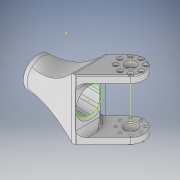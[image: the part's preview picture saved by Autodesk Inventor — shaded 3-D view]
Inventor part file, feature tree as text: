
AUTODESK INVENTOR PART (.ipt)
format: ipt  version: 2019 (Build 230136000, 136)  size: 1,101,312 bytes
history: native  units: mm
features: sketch x23, projected_geometry x19, extrude x16, plane x7, mirror x4, chamfer x4, fillet x4, other x4, loft x2, reference x2, pattern_circular x1, thicken_offset x1
ambient origin geometry x8: Origin, YZ Plane, XZ Plane, XY Plane, X Axis, Y Axis, Z Axis, Center Point
bodies: Solid1 (feature_tree)
feature tree (87):
  plane  "Work Plane1"
  plane  "Work Plane2"
  extrude  "Extrusion1"  Depth=23.0mm
  plane  "Work Plane5"
  extrude  "Extrusion2"  Depth=2.2mm
  extrude  "Extrusion3"  Depth=2.2mm
  mirror  "Mirror1"
  extrude  "Extrusion6"  Depth=2.2mm
  extrude  "Extrusion5"  Depth=2.2mm
  extrude  "Extrusion7"  Depth=7.0mm TaperAngle=0.0deg
  mirror  "Mirror2"
  extrude  "Extrusion8"  Depth=40.0mm
  extrude  "Extrusion9"  Depth=40.0mm
  mirror  "Mirror3"
  sketch  "Sketch10"  dims[d41=4.0mm d42=2.8mm]
  plane  "Work Plane8"
  extrude  "Extrusion11"  Depth=2.8mm
  extrude  "Extrusion12"  Depth=2.8mm
  extrude  "Extrusion13"  Depth=2.8mm
  sketch  "Sketch19"  dims[d49=2.8mm d50=2.0mm d51=0.0mm]
  plane  "Work Plane10"
  plane  "Work Plane9"
  sketch  "Sketch22"  dims[d52=45.5mm d53=4.0mm]
  sketch  "Sketch23"  dims[d54=45.5mm]
  plane  "Work Plane11"
  loft  "Loft3"
  extrude  "Extrusion15"  Depth=2.0mm TaperAngle=0.0deg
  extrude  "Extrusion16"  Depth=4.0mm
  chamfer  "Chamfer1"  Distance=4.0mm
  fillet  "Fillet17"  Radius=2.0mm
  fillet  "Fillet20"  Radius=5.2mm
  chamfer  "Chamfer2"  Distance=2.0mm
  fillet  "Fillet22"  Radius=2.5mm
  other  "Work Axis1"
  pattern_circular  "Circular Pattern1"  Angle=135.0deg  [1 undecoded]
  mirror  "Mirror4"
  extrude  "Extrusion17"  Depth=10.0mm
  chamfer  "Chamfer3"  Distance=5.2mm
  thicken_offset  "Thicken2"
  extrude  "Extrusion19"  Depth=10.0mm
  sketch  "Sketch31"  dims[d66=5.2mm]
  sketch  "Sketch32"  dims[d67=5.2mm]
  loft  "Loft4"
  extrude  "Extrusion21"  Depth=10.0mm
  fillet  "Fillet25"  Radius=5.5mm
  chamfer  "Chamfer4"  Distance=2.0mm
  sketch  "Sketch1"  dims[d0=44.5mm d1=23.0mm]
  sketch  "Sketch2"  dims[d2=2.2mm d3=2.2mm]
  projected_geometry  "Projected Loop1"
  sketch  "Sketch3"  dims[d4=2.2mm d5=2.2mm]
  projected_geometry  "Projected Loop2"
  sketch  "Sketch5"  dims[d6=2.2mm d7=2.2mm]
  reference  "Reference9"
  sketch  "Sketch6"  dims[d8=2.2mm d9=2.2mm]
  projected_geometry  "Projected Loop3"
  sketch  "Sketch7"  dims[d10=4.0mm d11=0.0mm d17=7.0mm d18=0.0mm]
  projected_geometry  "Projected Loop4"
  projected_geometry  "Projected Loop5"
  projected_geometry  "Projected Loop6"
  sketch  "Sketch8"  dims[d25=2.0mm d26=0.0mm d38=40.0mm]
  reference  "Reference10"
  projected_geometry  "Projected Loop7"
  projected_geometry  "Projected Loop8"
  sketch  "Sketch9"  dims[d39=4.0mm d40=40.0mm]
  projected_geometry  "Projected Loop9"
  projected_geometry  "Projected Loop10"
  sketch  "Sketch11"  dims[d43=2.8mm d44=2.8mm]
  projected_geometry  "Projected Loop11"
  projected_geometry  "Projected Loop12"
  sketch  "Sketch12"  dims[d45=2.8mm d46=2.8mm]
  projected_geometry  "Projected Loop13"
  sketch  "Sketch13"  dims[d47=2.8mm d48=2.8mm]
  projected_geometry  "Projected Loop14"
  sketch  "Sketch26"  dims[d55=4.0mm d56=4.0mm d57=0.0mm d58=2.0mm d59=0.0mm d61=5.2mm]
  other  "Edges3"
  sketch  "Sketch27"  dims[d62=5.2mm]
  projected_geometry  "Projected Loop18"
  sketch  "Sketch28"  dims[d63=5.2mm]
  projected_geometry  "Projected Loop19"
  sketch  "Sketch29"  dims[d64=5.2mm]
  sketch  "Sketch30"  dims[d65=5.2mm]
  other  "Edges4"
  other  "Edges5"
  sketch  "Sketch34"  dims[d68=5.2mm d69=2.0mm d70=0.0mm d71=2.5mm d78=135.0deg d79=5.2mm d80=5.2mm d81=5.2mm d82=5.2mm d83=5.2mm d85=5.5mm d86=2.0mm d87=20.0mm d88=14.827mm d89=40.0mm d90=10.0mm d91=0.0mm d92=27.2mm d93=31.0mm d96=4.0mm d97=0.0mm d98=4.0mm d99=0.0mm d100=4.0mm d101=0.0mm d131=-25.0mm d144=30.0mm d145=28.0mm d146=0.0mm d147=90.0deg d148=0.0mm d149=90.0deg d150=0.0mm d151=90.0deg d154=10.0mm d155=0.0mm d156=10.0mm d157=0.0mm d158=2.0mm d159=2.0mm d160=45.0deg d162=3.0mm d165=1.0mm d167=4.0mm d168=2.0mm d169=45.0deg d170=6.0mm d173=20.0mm d174=360.0deg d178=11.2mm d179=10.0mm d180=0.0mm d181=1.0mm d182=2.0mm d183=45.0deg d185=1.0mm d186=1.0mm d187=4.1mm d194=10.999993mm d195=80.0mm d197=360.0deg d199=10.0mm d200=0.0mm d201=0.0mm d202=90.0deg d203=0.0mm d204=90.0deg d207=4.0mm d208=0.0mm d209=2.0mm d210=11.2mm d211=0.5mm d212=2.0mm d213=45.0deg]
  projected_geometry  "Projected Loop23"
  projected_geometry  "Projected Loop24"
  projected_geometry  "Projected Loop25"
note: 1 required parameter value undecoded (feature->parameter linkage not recoverable at this tier; creation-order binding heuristic only, values carry confidence <= 0.55)
